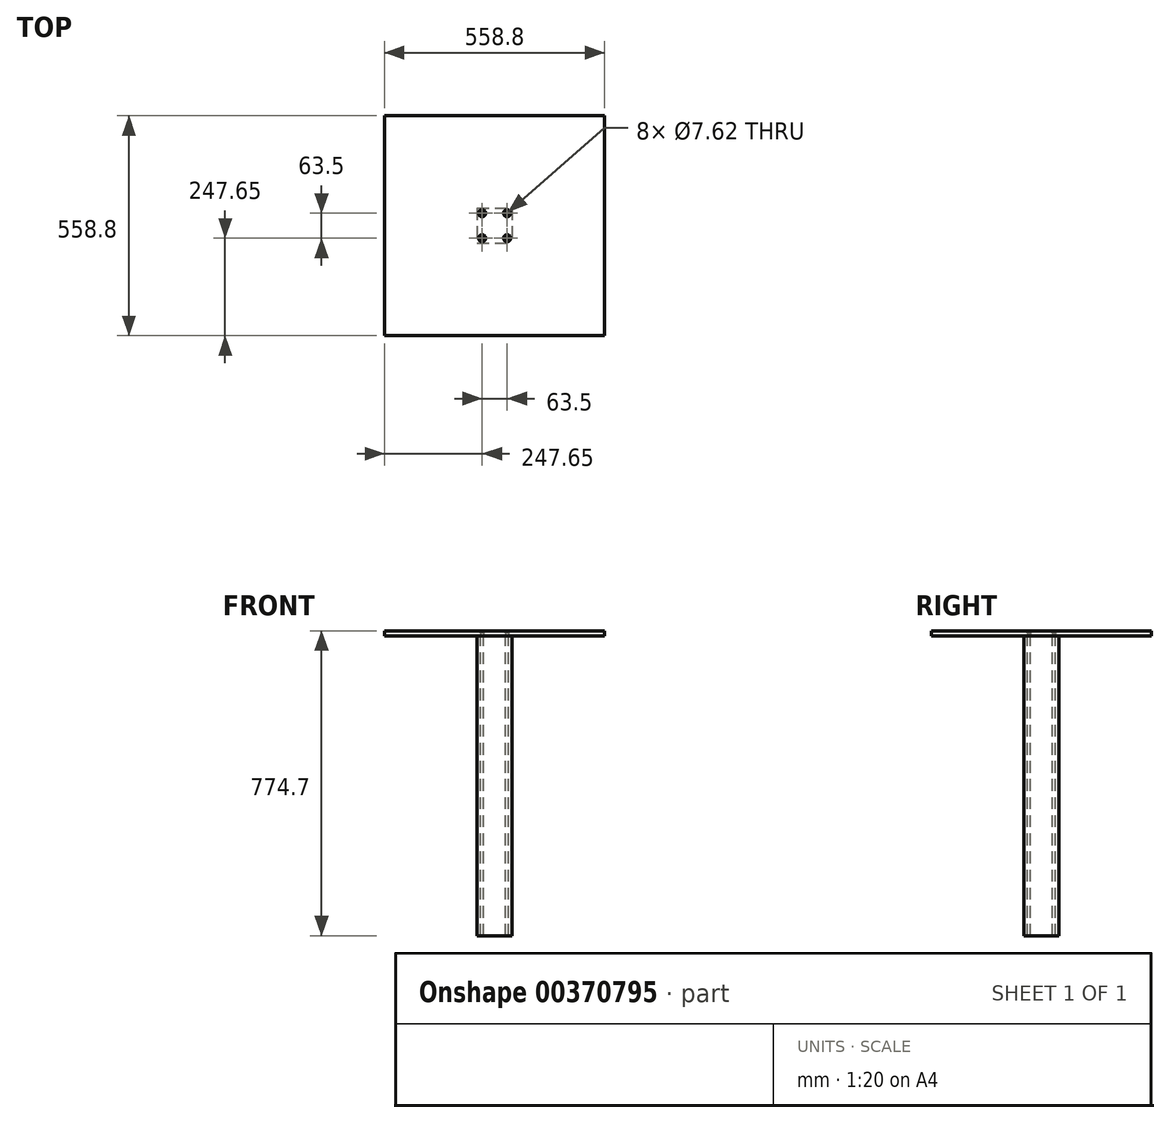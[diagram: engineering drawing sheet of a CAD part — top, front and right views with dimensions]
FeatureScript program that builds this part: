
annotation { "Feature Type Name" : "Feature", "Feature Type Description" : "" }
export const myFeature = defineFeature(function(context is Context, id is Id, definition is map)
    precondition{}
    {
        {
            var Q0;
            Q0=qCreatedBy(makeId("Top.planeOp"),FACE);
            var sketch = newSketch(context, id + "F0", { "sketchPlane" : qUnion([Q0])});
            skLineSegment(sketch, "E0", {"start": v(-646.32, 0) * mm, "end": v(646.32, 0) * mm, "construction": true});
            skLineSegment(sketch, "E1", {"start": v(0, 558.8) * mm, "end": v(0, -582.37) * mm, "construction": true});
            skPoint(sketch, "E1.endSnap0", {"position": v(0, 0) * mm});
            skLineSegment(sketch, "E2.bottom", {"start": v(-279.4, 279.4) * mm, "end": v(279.4, 279.4) * mm});
            skLineSegment(sketch, "E2.top", {"start": v(-279.4, -279.4) * mm, "end": v(279.4, -279.4) * mm});
            skLineSegment(sketch, "E2.left", {"start": v(-279.4, 279.4) * mm, "end": v(-279.4, -279.4) * mm});
            skLineSegment(sketch, "E2.right", {"start": v(279.4, 279.4) * mm, "end": v(279.4, -279.4) * mm});
            skLineSegment(sketch, "E3.bottom", {"start": v(-44.45, 44.45) * mm, "end": v(44.45, 44.45) * mm});
            skLineSegment(sketch, "E3.top", {"start": v(-44.45, -44.45) * mm, "end": v(44.45, -44.45) * mm});
            skLineSegment(sketch, "E3.left", {"start": v(-44.45, 44.45) * mm, "end": v(-44.45, -44.45) * mm});
            skLineSegment(sketch, "E3.right", {"start": v(44.45, 44.45) * mm, "end": v(44.45, -44.45) * mm});
            skLineSegment(sketch, "E4", {"start": v(-44.45, -44.45) * mm, "end": v(44.45, 44.45) * mm, "construction": true});
            skLineSegment(sketch, "E5", {"start": v(44.45, -44.45) * mm, "end": v(-44.45, 44.45) * mm, "construction": true});
            skCircle(sketch, "E6", {"center": v(-31.75, 31.75) * mm, "radius": 3.81 * mm});
            skCircle(sketch, "E7.MirrorC", {"center": v(31.75, -31.75) * mm, "radius": 3.81 * mm});
            skCircle(sketch, "E8.MirrorC", {"center": v(31.75, 31.75) * mm, "radius": 3.81 * mm});
            skCircle(sketch, "E9.MirrorC", {"center": v(-31.75, -31.75) * mm, "radius": 3.81 * mm});
            skSolve(sketch);
        }
        {
            var Q0;
            Q0=makeQuery(id+"F0.imprint","IMPRINT",FACE,{"disambiguationData":[TD([[makeQuery(id+"F0.imprint","IMPRINT",EDGE,{"derivedFrom":sQuery(id+"F0.wireOp",EDGE,"E2.bottom")}),-1.0]])]});
            var Q1;
            Q1=makeQuery(id+"F0.imprint","IMPRINT",FACE,{"disambiguationData":[TD([[makeQuery(id+"F0.imprint","IMPRINT",EDGE,{"derivedFrom":sQuery(id+"F0.wireOp",EDGE,"E3.bottom")}),-1.0]])]});
            extrude(context, id + "F1", {"entities" : qUnion([Q0, Q1]), "depth" : 12.7 * mm});
        }
        {
            var Q0;
            Q0=makeQuery(id+"F1.opExtrude","CAP_EDGE",EDGE,{"disambiguationData":[OSD([sQuery(id+"F0.wireOp",EDGE,"E9.MirrorC")])],"isStart":false});
            var Q1;
            Q1=makeQuery(id+"F1.opExtrude","CAP_EDGE",EDGE,{"disambiguationData":[OSD([sQuery(id+"F0.wireOp",EDGE,"E7.MirrorC")])],"isStart":false});
            var Q2;
            Q2=makeQuery(id+"F1.opExtrude","CAP_EDGE",EDGE,{"disambiguationData":[OSD([sQuery(id+"F0.wireOp",EDGE,"E8.MirrorC")])],"isStart":false});
            var Q3;
            Q3=makeQuery(id+"F1.opExtrude","CAP_EDGE",EDGE,{"disambiguationData":[OSD([sQuery(id+"F0.wireOp",EDGE,"E6")])],"isStart":false});
            chamfer(context, id + "F2", {"entities" : qUnion([Q0, Q1, Q2, Q3]), "width" : 5.08 * mm, "tangentPropagation" : true});
        }
        {
            var Q0;
            Q0=makeQuery(id+"F0.imprint","IMPRINT",FACE,{"disambiguationData":[TD([[makeQuery(id+"F0.imprint","IMPRINT",EDGE,{"derivedFrom":sQuery(id+"F0.wireOp",EDGE,"E3.bottom")}),-1.0]])]});
            extrude(context, id + "F3", {"entities" : qUnion([Q0]), "oppositeDirection" : true, "depth" : 762 * mm});
        }
    });
